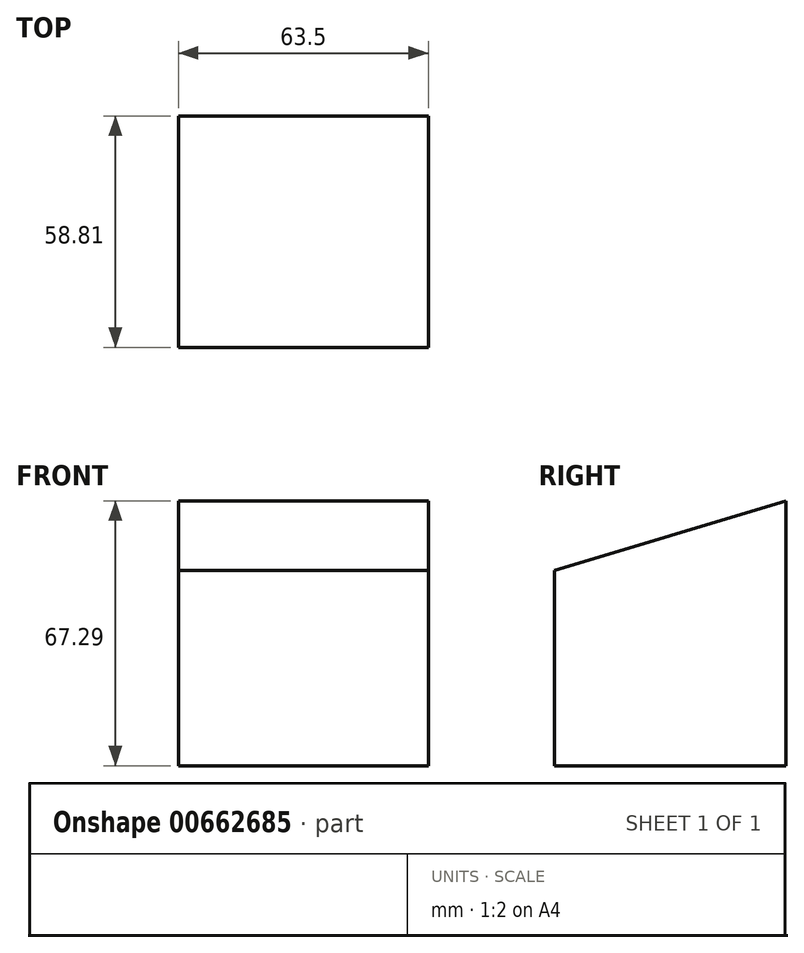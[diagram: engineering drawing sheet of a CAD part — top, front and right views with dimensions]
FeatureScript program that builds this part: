
annotation { "Feature Type Name" : "Feature", "Feature Type Description" : "" }
export const myFeature = defineFeature(function(context is Context, id is Id, definition is map)
    precondition{}
    {
        {
            var Q0;
            Q0=qCreatedBy(makeId("Right.planeOp"),FACE);
            var sketch = newSketch(context, id + "F0", { "sketchPlane" : qUnion([Q0])});
            skLineSegment(sketch, "E0", {"start": v(-31.75, -25.8) * mm, "end": v(27.06, -25.8) * mm});
            skLineSegment(sketch, "E1", {"start": v(-31.75, -25.8) * mm, "end": v(-31.75, 23.81) * mm});
            skLineSegment(sketch, "E2", {"start": v(27.06, -25.8) * mm, "end": v(27.06, 41.5) * mm});
            skLineSegment(sketch, "E3", {"start": v(27.06, 41.5) * mm, "end": v(-31.75, 23.81) * mm});
            skSolve(sketch);
        }
        {
            var Q0;
            Q0=makeQuery(id+"F0.imprint","IMPRINT",FACE,{"disambiguationData":[TD([[makeQuery(id+"F0.imprint","IMPRINT",EDGE,{"derivedFrom":sQuery(id+"F0.wireOp",EDGE,"E0")}),1.0]])]});
            extrude(context, id + "F1", {"entities" : qUnion([Q0]), "depth" : 63.5 * mm, "offsetDistance" : 25.4 * mm});
        }
    });
